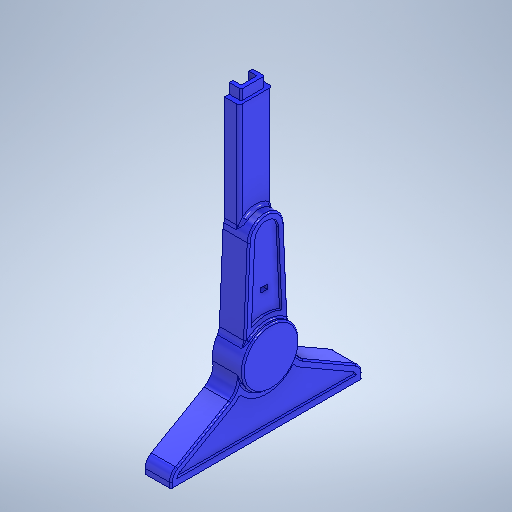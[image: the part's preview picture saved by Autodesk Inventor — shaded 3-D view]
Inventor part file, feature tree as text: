
AUTODESK INVENTOR PART (.ipt)
format: ipt  version: 2025.1 (Build 291241020, 241B)  size: 697,856 bytes
history: native  units: in
note: dims shown in document units (in); Inventor stores cm internally (conversion verified against a paired STEP export)
features: hole x1, sketch x1, other x1
ambient origin geometry x8: Origin, YZ Plane, XZ Plane, XY Plane, X Axis, Y Axis, Z Axis, Center Point
bodies: Solid1 (feature_tree)
feature tree (3):
  hole  "Hole1"  [1 undecoded]
  sketch  "Sketch1"  dims[d0=2.3622in d1=0.537in d2=4.0in d3=0.2685in d5=0.1969in d6=0.2362in d7=0.1575in d8=0.0787in d9=90.0deg d10=0.315in d11=0.8108in d12=2.3622in d13=0.2685in]
  other  "LEG"
note: 1 required parameter value undecoded (feature->parameter linkage not recoverable at this tier; creation-order binding heuristic only, values carry confidence <= 0.55)
